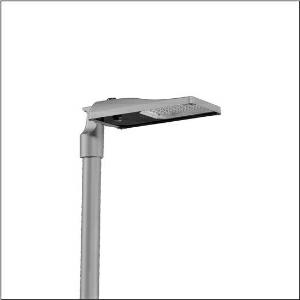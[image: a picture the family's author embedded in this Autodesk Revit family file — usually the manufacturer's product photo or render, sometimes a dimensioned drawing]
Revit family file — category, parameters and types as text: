
# Revit family: streetlight_sl_31_mini___st1_0a_5xh6d3at08ja_2b3a
name_source: partatom
category: Lighting Fixtures
units: mm (PartAtom-declared; Revit-internal decimal feet)

## family parameters
Cut with Voids When Loaded = No
Host = Face
Light Source = No
Part Type = Normal
Room Calculation Point = No
Round Connector Dimension = Use Diameter
Shared = No

## types (1)
- --- (1 x LED, 12270 lm, 82.5 W, 3000K)
    Apparent Load = 83 VA
    CIE Flux Codes = 40 73 97 100 100
    Color Rendering = 70
    Color Temperature = 3000K
    Default Elevation = 1800 mm
    Description = Streetlight SL 31 mini D4i mast luminaire for post-top, side-entry; light control with lens of PMMA; light distribution: ST1.0a, direct asymmetric distribution, for standard-compliant lighting for roads and squares; LED: luminous flux: 12.270lm, light colour: 730, colour temperature: 3000K; luminous efficacy: 148,7lm/W; control: pre-setting: logarithmic dimming characteristic, flexible luminous flux parameterisation, time-dependent luminous flux control, constant luminous flux control, power reduction, intelligent temperature release in ECG and LED module, overheat protection; luminaire housing, of diecast aluminium, SITECO metallic grey (DB 702S), corrosivity category C5 high according to DIN EN ISO 12944; cover of toughened safety glass, transparent, opened without tools; mast flange of diecast aluminium, SITECO metallic grey (DB 702S), spigot size: 76/60mm, mast flange included unmounted; cable length: 10,5m, connection cable pre-assembled; mains connection: 220..240V, AC, 50/60Hz; power consumption (at start of service life): 82,5W / (at end of service life): 90,1W / (with reduced operation 50%): 36,8W; protection rating (complete): IP66; insulation class (complete): insulation class II (safety insulation); impact resistance: IK09; certification: CE, ENEC, ENEC+, VDE, UKCA, ZD4i; permissible operating ambient temperature for outdoor applications: -40..+50°C; packaging unit: 1 piece

Light Distribution: ST1.0a
    Height = 76 mm
    Lamp = 1 x LED
    Lamp Light Flux = 12270 lm
    Lamp Power = 82.5 W
    Lamp count = 1
    Length = 547 mm
    Luminous efficacy = 149 lm/W
    Manufacturer = Siteco
    ModVariant = No
    Model = 5XH6D3AT08JA
    Number of Poles = 1
    OnlyDefault = Yes
    Power Factor = 1
    Product Name = Streetlight SL 31 mini | ST1.0a
    Product group = mast luminaire | pylon top
    ProductGroupID = 6100
    Protection Class = Protection class II
    Protection Degree = IP 66
    RLX_Detail_Level = 1
    RLX_Emergency_Light_Flux = 0 lm
    RLX_Emergency_Type = 0
    RLX_Emergency_Type_DB = No
    RlxData = <blob elided: 39813 chars, md5=9e3188ee>
    Socket = socket
    Standby Power = 0 W
    System Light Flux = 12270 lm
    System Power = 83 W
    Type Comments = factory setting: luminous flux: 100 % | dim-lin: 254 | 870 mA
    Type Image = l_1300332.jpg
    URL = http://relux.com
    VarID = @adj_057035
    Voltage = 0 V
    Weight = 0.00 kg
    Width = 265 mm

## geometry (parser evidence)
native form markers: Blend x4, Sweep x10
no freeform markers — native parametric forms only
